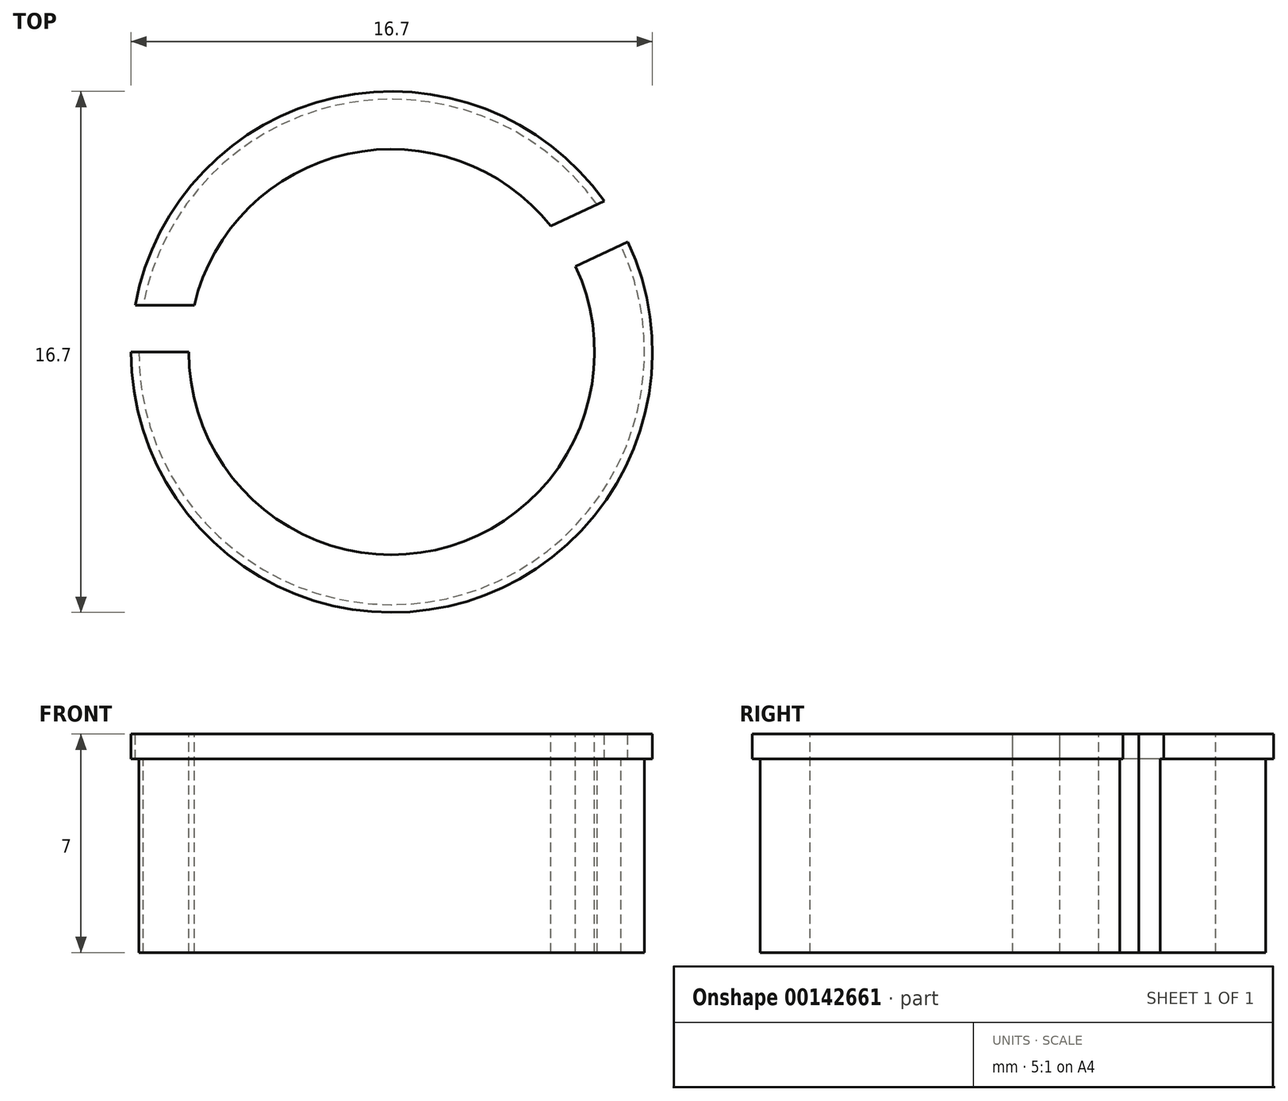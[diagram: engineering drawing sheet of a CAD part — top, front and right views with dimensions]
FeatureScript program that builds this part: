
annotation { "Feature Type Name" : "Feature", "Feature Type Description" : "" }
export const myFeature = defineFeature(function(context is Context, id is Id, definition is map)
    precondition{}
    {
        {
            var Q0;
            Q0=qCreatedBy(makeId("Top.planeOp"),FACE);
            var sketch = newSketch(context, id + "F0", { "sketchPlane" : qUnion([Q0])});
            skCircle(sketch, "E0", {"center": v(0, 0) * mm, "radius": 8.35 * mm});
            skCircle(sketch, "E1", {"center": v(0, 0) * mm, "radius": 8.1 * mm});
            skCircle(sketch, "E2", {"center": v(0, 0) * mm, "radius": 6.5 * mm});
            skLineSegment(sketch, "E3", {"start": v(0, 0) * mm, "end": v(-12.75, 0) * mm});
            skLineSegment(sketch, "E4", {"start": v(0, 0) * mm, "end": v(10.34, 4.82) * mm});
            skLineSegment(sketch, "E5.0", {"start": v(-0.33, 1.5) * mm, "end": v(-12.75, 1.5) * mm});
            skLineSegment(sketch, "E5.1", {"start": v(-0.33, 1.5) * mm, "end": v(9.7, 6.18) * mm});
            skSolve(sketch);
        }
        {
            var Q0;
            {var subQ0=sQuery(id+"F0.wireOp",EDGE,"E4");var subQ1=sQuery(id+"F0.wireOp",EDGE,"E1");var subQ2=makeQuery(id+"F0.imprint","INTERSECT",VERTEX,{"derivedFrom":[subQ1,subQ0]});Q0=makeQuery(id+"F0.imprint","IMPRINT",FACE,{"disambiguationData":[TD([[makeQuery(id+"F0.imprint","IMPRINT",EDGE,{"disambiguationData":[TD([[subQ2,1.0]])],"derivedFrom":subQ1}),1.0]])]});}
            extrude(context, id + "F1", {"entities" : qUnion([Q0]), "oppositeDirection" : true, "depth" : 7 * mm});
        }
        {
            var Q0;
            {var subQ0=sQuery(id+"F0.wireOp",EDGE,"E4");var subQ1=sQuery(id+"F0.wireOp",EDGE,"E0");var subQ2=makeQuery(id+"F0.imprint","INTERSECT",VERTEX,{"derivedFrom":[subQ1,subQ0]});Q0=makeQuery(id+"F0.imprint","IMPRINT",FACE,{"disambiguationData":[TD([[makeQuery(id+"F0.imprint","IMPRINT",EDGE,{"disambiguationData":[TD([[subQ2,1.0]])],"derivedFrom":subQ1}),1.0]])]});}
            extrude(context, id + "F2", {"entities" : qUnion([Q0]), "operationType" : NewBodyOperationType.ADD, "oppositeDirection" : true, "depth" : .8 * mm});
        }
        {
            var Q0;
            {var subQ0=sQuery(id+"F0.wireOp",EDGE,"E5.1");var subQ1=sQuery(id+"F0.wireOp",EDGE,"E1");var subQ2=makeQuery(id+"F0.imprint","INTERSECT",VERTEX,{"derivedFrom":[subQ1,subQ0]});Q0=makeQuery(id+"F0.imprint","IMPRINT",FACE,{"disambiguationData":[TD([[makeQuery(id+"F0.imprint","IMPRINT",EDGE,{"disambiguationData":[TD([[subQ2,-1.0]])],"derivedFrom":subQ1}),1.0]])]});}
            extrude(context, id + "F3", {"entities" : qUnion([Q0]), "oppositeDirection" : true, "depth" : 7 * mm});
        }
        {
            var Q0;
            {var subQ0=sQuery(id+"F0.wireOp",EDGE,"E5.1");var subQ1=sQuery(id+"F0.wireOp",EDGE,"E0");var subQ2=makeQuery(id+"F0.imprint","INTERSECT",VERTEX,{"derivedFrom":[subQ1,subQ0]});Q0=makeQuery(id+"F0.imprint","IMPRINT",FACE,{"disambiguationData":[TD([[makeQuery(id+"F0.imprint","IMPRINT",EDGE,{"disambiguationData":[TD([[subQ2,-1.0]])],"derivedFrom":subQ1}),1.0]])]});}
            extrude(context, id + "F4", {"entities" : qUnion([Q0]), "operationType" : NewBodyOperationType.ADD, "oppositeDirection" : true, "depth" : .8 * mm});
        }
    });
